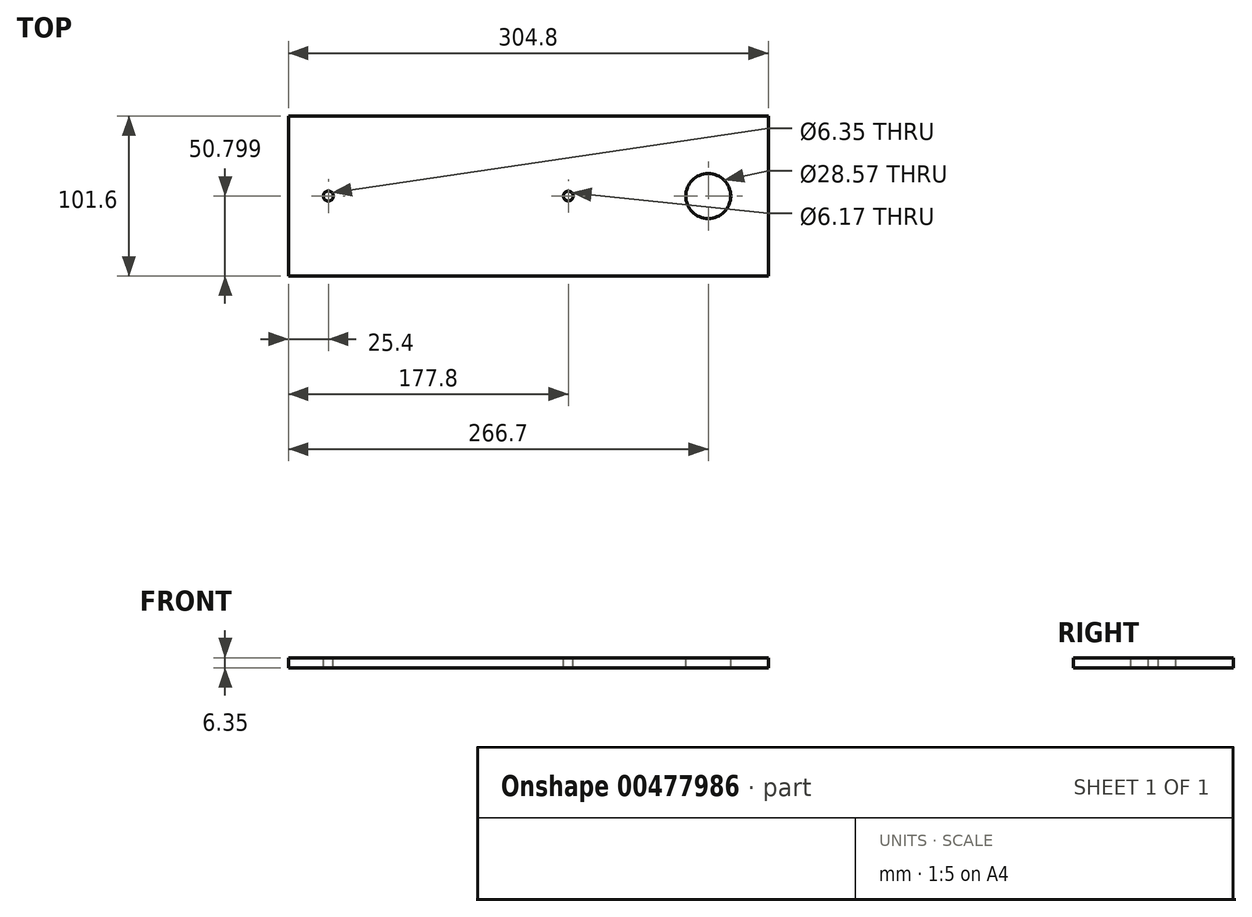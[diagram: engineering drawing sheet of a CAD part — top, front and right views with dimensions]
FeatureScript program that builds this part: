
annotation { "Feature Type Name" : "Feature", "Feature Type Description" : "" }
export const myFeature = defineFeature(function(context is Context, id is Id, definition is map)
    precondition{}
    {
        {
            var Q0;
            Q0=qCreatedBy(makeId("Top.planeOp"),FACE);
            var sketch = newSketch(context, id + "F0", { "sketchPlane" : qUnion([Q0])});
            skLineSegment(sketch, "E0.bottom", {"start": v(-72.69, 42.63) * mm, "end": v(232.11, 42.63) * mm});
            skLineSegment(sketch, "E0.top", {"start": v(-72.69, -58.97) * mm, "end": v(232.11, -58.97) * mm});
            skLineSegment(sketch, "E0.left", {"start": v(-72.69, 42.63) * mm, "end": v(-72.69, -58.97) * mm});
            skLineSegment(sketch, "E0.right", {"start": v(232.11, 42.63) * mm, "end": v(232.11, -58.97) * mm});
            skSolve(sketch);
        }
        {
            var Q0;
            Q0=makeQuery(id+"F0.imprint","IMPRINT",FACE,{"disambiguationData":[TD([[makeQuery(id+"F0.imprint","IMPRINT",EDGE,{"derivedFrom":sQuery(id+"F0.wireOp",EDGE,"E0.bottom")}),-1.0]])]});
            extrude(context, id + "F1", {"entities" : qUnion([Q0]), "depth" : 6.35 * mm});
        }
        {
            var Q0;
            Q0=makeQuery(id+"F1.opExtrude","CAP_FACE",FACE,{"disambiguationData":[OSD([sQuery(id+"F0.wireOp",EDGE,"E0.bottom"),sQuery(id+"F0.wireOp",EDGE,"E0.top"),sQuery(id+"F0.wireOp",EDGE,"E0.left"),sQuery(id+"F0.wireOp",EDGE,"E0.right")])],"isStart":false});
            var sketch = newSketch(context, id + "F2", { "sketchPlane" : qUnion([Q0])});
            skPoint(sketch, "E1", {"position": v(-47.29, -8.17) * mm});
            skCircle(sketch, "E2", {"center": v(-47.29, -8.17) * mm, "radius": 3.18 * mm});
            skSolve(sketch);
        }
        {
            var Q0;
            Q0=makeQuery(id+"F2.imprint","IMPRINT",FACE,{"disambiguationData":[TD([[makeQuery(id+"F2.imprint","IMPRINT",EDGE,{"derivedFrom":sQuery(id+"F2.wireOp",EDGE,"E2")}),1.0]])]});
            extrude(context, id + "F3", {"entities" : qUnion([Q0]), "operationType" : NewBodyOperationType.REMOVE, "oppositeDirection" : true, "depth" : 6.35 * mm});
        }
        {
            var Q0;
            Q0=makeQuery(id+"F2.imprint","IMPRINT",FACE,{"disambiguationData":[TD([[makeQuery(id+"F2.imprint","IMPRINT",EDGE,{"derivedFrom":sQuery(id+"F2.wireOp",EDGE,"E2")}),-1.0]])]});
            var sketch = newSketch(context, id + "F4", { "sketchPlane" : qUnion([Q0])});
            skCircle(sketch, "E3", {"center": v(194.01, -8.17) * mm, "radius": 14.29 * mm});
            skSolve(sketch);
        }
        {
            var Q0;
            Q0=makeQuery(id+"F4.imprint","IMPRINT",FACE,{"disambiguationData":[TD([[makeQuery(id+"F4.imprint","IMPRINT",EDGE,{"derivedFrom":sQuery(id+"F4.wireOp",EDGE,"E3")}),1.0]])]});
            extrude(context, id + "F5", {"entities" : qUnion([Q0]), "operationType" : NewBodyOperationType.REMOVE, "oppositeDirection" : true, "depth" : 6.35 * mm});
        }
        {
            var Q0;
            Q0=makeQuery(id+"F1.opExtrude","CAP_FACE",FACE,{"disambiguationData":[OSD([sQuery(id+"F0.wireOp",EDGE,"E0.bottom"),sQuery(id+"F0.wireOp",EDGE,"E0.top"),sQuery(id+"F0.wireOp",EDGE,"E0.left"),sQuery(id+"F0.wireOp",EDGE,"E0.right")])],"isStart":false});
            var sketch = newSketch(context, id + "F6", { "sketchPlane" : qUnion([Q0])});
            skCircle(sketch, "E4", {"center": v(105.11, -8.17) * mm, "radius": 3.09 * mm});
            skSolve(sketch);
        }
        {
            var Q0;
            Q0=makeQuery(id+"F6.imprint","IMPRINT",FACE,{"disambiguationData":[TD([[makeQuery(id+"F6.imprint","IMPRINT",EDGE,{"derivedFrom":sQuery(id+"F6.wireOp",EDGE,"E4")}),1.0]])]});
            extrude(context, id + "F7", {"entities" : qUnion([Q0]), "operationType" : NewBodyOperationType.REMOVE, "oppositeDirection" : true, "depth" : 6.35 * mm});
        }
    });
